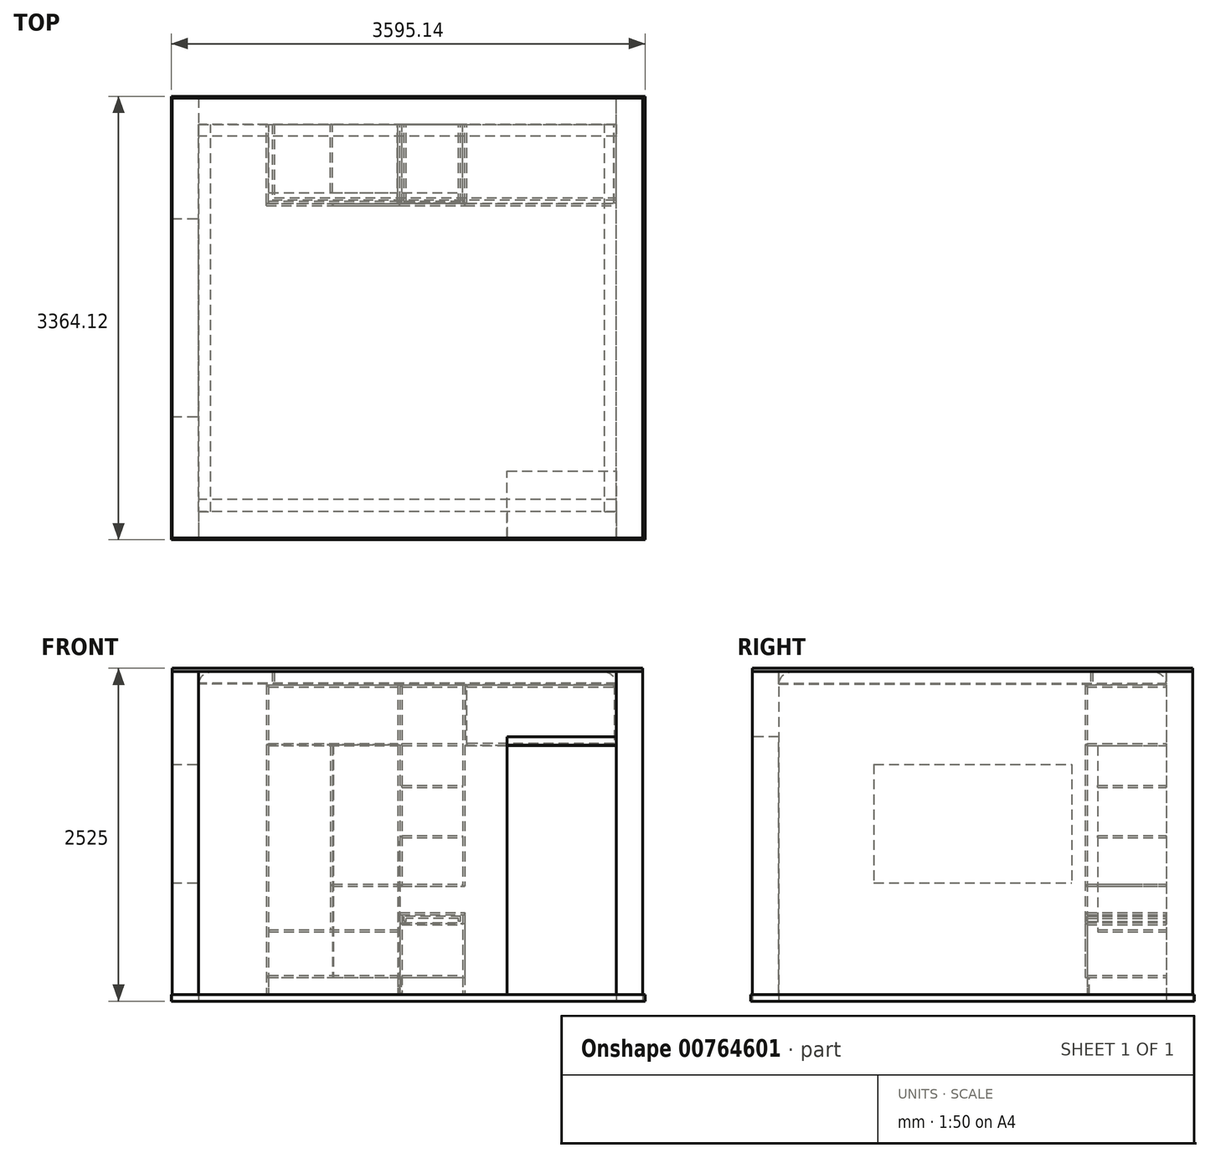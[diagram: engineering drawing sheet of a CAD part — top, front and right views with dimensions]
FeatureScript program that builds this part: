
annotation { "Feature Type Name" : "Feature", "Feature Type Description" : "" }
export const myFeature = defineFeature(function(context is Context, id is Id, definition is map)
    precondition{}
    {
        {
            var Q0;
            Q0=qCreatedBy(makeId("Top.planeOp"),FACE);
            var sketch = newSketch(context, id + "F0", { "sketchPlane" : qUnion([Q0])});
            skLineSegment(sketch, "E0.0.0", {"start": v(-1555, 1015.23) * mm, "end": v(1615, 1015.23) * mm});
            skLineSegment(sketch, "E0.0.1", {"start": v(1615, 1015.23) * mm, "end": v(1615, 1215.23) * mm});
            skLineSegment(sketch, "E0.0.2", {"start": v(1615, 1215.23) * mm, "end": v(-1555, 1215.23) * mm});
            skLineSegment(sketch, "E0.0.3", {"start": v(-1555, 1215.23) * mm, "end": v(-1555, 1015.23) * mm});
            skLineSegment(sketch, "E1.bottom", {"start": v(1815, 1215.23) * mm, "end": v(1615, 1215.23) * mm});
            skLineSegment(sketch, "E1.top", {"start": v(1815, -2124.77) * mm, "end": v(1615, -2124.77) * mm});
            skLineSegment(sketch, "E1.left", {"start": v(1815, 1215.23) * mm, "end": v(1815, -2124.77) * mm});
            skLineSegment(sketch, "E1.right", {"start": v(1615, 1215.23) * mm, "end": v(1615, -2124.77) * mm});
            skLineSegment(sketch, "E2.bottom", {"start": v(-1555, 1215.23) * mm, "end": v(-1755, 1215.23) * mm});
            skLineSegment(sketch, "E2.top", {"start": v(-1555, -2124.77) * mm, "end": v(-1755, -2124.77) * mm});
            skLineSegment(sketch, "E2.left", {"start": v(-1555, 1215.23) * mm, "end": v(-1555, -2124.77) * mm});
            skLineSegment(sketch, "E2.right", {"start": v(-1755, 1215.23) * mm, "end": v(-1755, -2124.77) * mm});
            skLineSegment(sketch, "E3.0.0", {"start": v(-1555, -2124.77) * mm, "end": v(1613.37, -2124.77) * mm});
            skLineSegment(sketch, "E3.0.1", {"start": v(1613.37, -2124.77) * mm, "end": v(1613.37, -1924.77) * mm});
            skLineSegment(sketch, "E3.0.2", {"start": v(1613.37, -1924.77) * mm, "end": v(-1555, -1924.77) * mm});
            skLineSegment(sketch, "E3.0.3", {"start": v(-1555, -1924.77) * mm, "end": v(-1555, -2124.77) * mm});
            skSolve(sketch);
        }
        {
            var Q0;
            {var subQ2=sQuery(id+"F0.wireOp",EDGE,"E1.bottom");Q0=makeQuery(id+"F0.imprint","IMPRINT",FACE,{"disambiguationData":[TD([[makeQuery(id+"F0.imprint","IMPRINT",EDGE,{"derivedFrom":subQ2}),1.0]])]});}
            var Q1;
            {var subQ5=sQuery(id+"F0.wireOp",EDGE,"E2.bottom");Q1=makeQuery(id+"F0.imprint","IMPRINT",FACE,{"disambiguationData":[TD([[makeQuery(id+"F0.imprint","IMPRINT",EDGE,{"derivedFrom":subQ5}),1.0]])]});}
            extrude(context, id + "F1", {"entities" : qUnion([Q0, Q1]), "depth" : 2500 * mm, "offsetDistance" : 25 * mm});
        }
        {
            var Q0;
            {var subQ0=sQuery(id+"F0.wireOp",EDGE,"E0.0.0");Q0=makeQuery(id+"F0.imprint","IMPRINT",FACE,{"disambiguationData":[TD([[makeQuery(id+"F0.imprint","IMPRINT",EDGE,{"derivedFrom":subQ0}),1.0]])]});}
            var Q1;
            Q1=makeQuery(id+"F0.imprint","IMPRINT",FACE,{"disambiguationData":[TD([[makeQuery(id+"F0.imprint","IMPRINT",EDGE,{"derivedFrom":sQuery(id+"F0.wireOp",EDGE,"E3.0.0")}),1.0]])]});
            extrude(context, id + "F2", {"entities" : qUnion([Q0, Q1]), "depth" : 2500 * mm, "offsetDistance" : 25 * mm});
        }
        {
            var Q0;
            Q0=makeQuery(id+"F1.opExtrude","SWEPT_FACE",FACE,{"disambiguationData":[OSD([sQuery(id+"F0.wireOp",EDGE,"E2.left"),sQuery(id+"F0.wireOp",EDGE,"E3.0.3")])]});
            var sketch = newSketch(context, id + "F3", { "sketchPlane" : qUnion([Q0])});
            skLineSegment(sketch, "E4.bottom", {"start": v(-1202.13, 1797) * mm, "end": v(297.87, 1797) * mm});
            skLineSegment(sketch, "E4.top", {"start": v(-1202.13, 897) * mm, "end": v(297.87, 897) * mm});
            skLineSegment(sketch, "E4.left", {"start": v(-1202.13, 1797) * mm, "end": v(-1202.13, 897) * mm});
            skLineSegment(sketch, "E4.right", {"start": v(297.87, 1797) * mm, "end": v(297.87, 897) * mm});
            skSolve(sketch);
        }
        {
            var Q0;
            Q0=makeQuery(id+"F3.imprint","IMPRINT",FACE,{"disambiguationData":[TD([[makeQuery(id+"F3.imprint","IMPRINT",EDGE,{"derivedFrom":sQuery(id+"F3.wireOp",EDGE,"E4.bottom")}),-1.0]])]});
            extrude(context, id + "F4", {"entities" : qUnion([Q0]), "operationType" : NewBodyOperationType.REMOVE, "oppositeDirection" : true, "depth" : 620 * mm, "offsetDistance" : 25 * mm});
        }
        {
            var Q0;
            {var subQ0=sQuery(id+"F0.wireOp",EDGE,"E0.0.0");Q0=makeQuery(id+"F0.imprint","IMPRINT",FACE,{"disambiguationData":[TD([[makeQuery(id+"F0.imprint","IMPRINT",EDGE,{"derivedFrom":subQ0}),1.0]])]});}
            var sketch = newSketch(context, id + "F5", { "sketchPlane" : qUnion([Q0])});
            skLineSegment(sketch, "E5.bottom", {"start": v(-1761.66, -2136.75) * mm, "end": v(1833.48, -2136.75) * mm});
            skLineSegment(sketch, "E5.top", {"start": v(-1761.66, 1227.37) * mm, "end": v(1833.48, 1227.37) * mm});
            skLineSegment(sketch, "E5.left", {"start": v(-1761.66, -2136.75) * mm, "end": v(-1761.66, 1227.37) * mm});
            skLineSegment(sketch, "E5.right", {"start": v(1833.48, -2136.75) * mm, "end": v(1833.48, 1227.37) * mm});
            skSolve(sketch);
        }
        {
            var Q0;
            Q0=makeQuery(id+"F5.imprint","IMPRINT",FACE,{"disambiguationData":[TD([[makeQuery(id+"F5.imprint","IMPRINT",EDGE,{"derivedFrom":sQuery(id+"F5.wireOp",EDGE,"E5.bottom")}),1.0]])]});
            extrude(context, id + "F6", {"entities" : qUnion([Q0]), "depth" : 50 * mm, "offsetDistance" : 25 * mm});
        }
        {
            var Q0;
            Q0=makeQuery(id+"F2.opExtrude","SWEPT_FACE",FACE,{"disambiguationData":[OSD([sQuery(id+"F0.wireOp",EDGE,"E0.0.0")])]});
            var sketch = newSketch(context, id + "F7", { "sketchPlane" : qUnion([Q0])});
            skLineSegment(sketch, "E6.bottom", {"start": v(-1555, 2500) * mm, "end": v(-1462.64, 2500) * mm});
            skLineSegment(sketch, "E6.left", {"start": v(-1555, 2500) * mm, "end": v(-1555, 2412.32) * mm});
            skFitSpline(sketch, "E7", {"points": [v(-1555, 2400.43) * mm, v(-1455, 2500) * mm], "startDerivative": vector(33.84, 289.83) * mm, "endDerivative": vector(27.08, 13.3) * mm});
            skArc(sketch, "E8.filletArc", {"start": v(-1555, 2412.32) * mm, "mid": v(-1554.18, 2411.42) * mm, "end": v(-1553.22, 2412.15) * mm});
            skArc(sketch, "E9.filletArc", {"start": v(-1462.48, 2498.21) * mm, "mid": v(-1461.75, 2499.18) * mm, "end": v(-1462.64, 2500) * mm});
            skLineSegment(sketch, "E10.bottom", {"start": v(1615, 2500) * mm, "end": v(1615, 2407.64) * mm});
            skLineSegment(sketch, "E10.left", {"start": v(1615, 2500) * mm, "end": v(1527.32, 2500) * mm});
            skFitSpline(sketch, "E11", {"points": [v(1515.43, 2500) * mm, v(1615, 2400) * mm], "startDerivative": vector(289.83, -33.84) * mm, "endDerivative": vector(13.3, -27.08) * mm});
            skArc(sketch, "E12.filletArc", {"start": v(1527.32, 2500) * mm, "mid": v(1526.42, 2499.18) * mm, "end": v(1527.15, 2498.22) * mm});
            skArc(sketch, "E13.filletArc", {"start": v(1613.22, 2407.48) * mm, "mid": v(1614.18, 2406.75) * mm, "end": v(1615, 2407.64) * mm});
            skSolve(sketch);
        }
        {
            var Q0;
            Q0 = qSketchRegion(id + "F7", true);
            extrude(context, id + "F8", {"entities" : qUnion([Q0]), "depth" : 2940 * mm, "offsetDistance" : 25 * mm});
        }
        {
            var Q0;
            Q0=makeQuery(id+"F1.opExtrude","SWEPT_FACE",FACE,{"disambiguationData":[OSD([sQuery(id+"F0.wireOp",EDGE,"E2.left"),sQuery(id+"F0.wireOp",EDGE,"E3.0.3")])]});
            var sketch = newSketch(context, id + "F9", { "sketchPlane" : qUnion([Q0])});
            skLineSegment(sketch, "E14.bottom", {"start": v(-1924.58, 2500) * mm, "end": v(-1832.23, 2500) * mm});
            skLineSegment(sketch, "E14.left", {"start": v(-1924.58, 2500) * mm, "end": v(-1924.58, 2412.32) * mm});
            skFitSpline(sketch, "E15", {"points": [v(-1924.58, 2400.43) * mm, v(-1824.58, 2500) * mm], "startDerivative": vector(33.84, 289.83) * mm, "endDerivative": vector(27.08, 13.3) * mm});
            skArc(sketch, "E16.filletArc", {"start": v(-1924.58, 2412.32) * mm, "mid": v(-1923.77, 2411.43) * mm, "end": v(-1922.8, 2412.15) * mm});
            skArc(sketch, "E17.filletArc", {"start": v(-1832.06, 2498.22) * mm, "mid": v(-1831.33, 2499.19) * mm, "end": v(-1832.23, 2500) * mm});
            skLineSegment(sketch, "E18.bottom", {"start": v(1014.88, 2500) * mm, "end": v(1014.88, 2407.64) * mm});
            skLineSegment(sketch, "E18.left", {"start": v(1014.88, 2500) * mm, "end": v(927.2, 2500) * mm});
            skFitSpline(sketch, "E19", {"points": [v(915.3, 2500) * mm, v(1014.88, 2400) * mm], "startDerivative": vector(289.83, -33.84) * mm, "endDerivative": vector(13.3, -27.08) * mm});
            skArc(sketch, "E20.filletArc", {"start": v(927.2, 2500) * mm, "mid": v(926.3, 2499.18) * mm, "end": v(927.03, 2498.22) * mm});
            skArc(sketch, "E21.filletArc", {"start": v(1013.1, 2407.48) * mm, "mid": v(1014.06, 2406.75) * mm, "end": v(1014.88, 2407.64) * mm});
            skSolve(sketch);
        }
        {
            var Q0;
            Q0 = qSketchRegion(id + "F9", true);
            extrude(context, id + "F10", {"entities" : qUnion([Q0]), "depth" : 3169.2 * mm, "offsetDistance" : 25 * mm});
        }
        {
            var Q0;
            Q0=makeQuery(id+"F2.opExtrude","SWEPT_FACE",FACE,{"disambiguationData":[OSD([sQuery(id+"F0.wireOp",EDGE,"E3.0.0")])]});
            var sketch = newSketch(context, id + "F11", { "sketchPlane" : qUnion([Q0])});
            skLineSegment(sketch, "E22.bottom", {"start": v(1613.37, 49.92) * mm, "end": v(785.99, 49.92) * mm});
            skLineSegment(sketch, "E22.top", {"start": v(1613.37, 2005.08) * mm, "end": v(785.99, 2005.08) * mm});
            skLineSegment(sketch, "E22.left", {"start": v(1613.37, 49.92) * mm, "end": v(1613.37, 2005.08) * mm});
            skLineSegment(sketch, "E22.right", {"start": v(785.99, 49.92) * mm, "end": v(785.99, 2005.08) * mm});
            skSolve(sketch);
        }
        {
            var Q0;
            Q0=makeQuery(id+"F11.imprint","IMPRINT",FACE,{"disambiguationData":[TD([[makeQuery(id+"F11.imprint","IMPRINT",EDGE,{"derivedFrom":sQuery(id+"F11.wireOp",EDGE,"E22.bottom")}),-1.0]])]});
            extrude(context, id + "F12", {"entities" : qUnion([Q0]), "operationType" : NewBodyOperationType.REMOVE, "oppositeDirection" : true, "depth" : 510 * mm, "offsetDistance" : 25 * mm});
        }
        {
            var Q0;
            Q0=makeQuery(id+"F2.opExtrude","CAP_FACE",FACE,{"disambiguationData":[OSD([sQuery(id+"F0.wireOp",EDGE,"E0.0.0"),sQuery(id+"F0.wireOp",EDGE,"E0.0.2"),sQuery(id+"F0.wireOp",EDGE,"E1.right"),sQuery(id+"F0.wireOp",EDGE,"E2.left")])],"isStart":false});
            var sketch = newSketch(context, id + "F13", { "sketchPlane" : qUnion([Q0])});
            skLineSegment(sketch, "E23.0", {"start": v(1815, 1215.23) * mm, "end": v(-1755, 1215.23) * mm});
            skLineSegment(sketch, "E24.0", {"start": v(1815, 1215.23) * mm, "end": v(1815, -2124.77) * mm});
            skLineSegment(sketch, "E25.0", {"start": v(-1755, -2124.77) * mm, "end": v(1815, -2124.77) * mm});
            skLineSegment(sketch, "E26.0", {"start": v(-1755, 1215.23) * mm, "end": v(-1755, -2124.77) * mm});
            skSolve(sketch);
        }
        {
            var Q0;
            Q0 = qSketchRegion(id + "F13", true);
            extrude(context, id + "F14", {"entities" : qUnion([Q0]), "depth" : 25 * mm, "offsetDistance" : 25 * mm});
        }
        {
            var Q0;
            Q0=makeQuery(id+"F2.opExtrude","SWEPT_FACE",FACE,{"disambiguationData":[OSD([sQuery(id+"F0.wireOp",EDGE,"E0.0.0")])]});
            var sketch = newSketch(context, id + "F15", { "sketchPlane" : qUnion([Q0])});
            skLineSegment(sketch, "E27", {"start": v(498.7, 98.2) * mm, "end": v(1598.7, 98.2) * mm});
            skLineSegment(sketch, "E28", {"start": v(-930.04, 98.4) * mm, "end": v(469.96, 98.4) * mm});
            skLineSegment(sketch, "E29", {"start": v(-930.56, 51.34) * mm, "end": v(-930.04, 1954.15) * mm});
            skLineSegment(sketch, "E30", {"start": v(-930.04, 1954.15) * mm, "end": v(-930.04, 2500) * mm});
            skSolve(sketch);
        }
        {
            var Q0;
            {var subQ0=sQuery(id+"F0.wireOp",EDGE,"E0.0.0");Q0=makeQuery(id+"F15.imprint","IMPRINT",FACE,{"disambiguationData":[TD([[makeQuery(id+"F15.imprint","IMPRINT",EDGE,{"derivedFrom":makeQuery(id+"F2.opExtrude","CAP_EDGE",EDGE,{"disambiguationData":[OSD([subQ0])],"isStart":true})}),1.0]])]});}
            var sketch = newSketch(context, id + "F16", { "sketchPlane" : qUnion([Q0])});
            skLineSegment(sketch, "E31.bottom", {"start": v(-1039.66, 2400.3) * mm, "end": v(-1023.66, 2400.3) * mm});
            skLineSegment(sketch, "E31.top", {"start": v(-1039.66, 50.3) * mm, "end": v(-1023.66, 50.3) * mm});
            skLineSegment(sketch, "E31.left", {"start": v(-1039.66, 2400.3) * mm, "end": v(-1039.66, 50.3) * mm});
            skLineSegment(sketch, "E31.right", {"start": v(-1023.66, 2400.3) * mm, "end": v(-1023.66, 50.3) * mm});
            skLineSegment(sketch, "E32.bottom", {"start": v(449.94, 2400.3) * mm, "end": v(466, 2400.3) * mm});
            skLineSegment(sketch, "E32.top", {"start": v(450, 50.3) * mm, "end": v(466, 50.3) * mm});
            skLineSegment(sketch, "E32.left", {"start": v(449.94, 2400.3) * mm, "end": v(449.98, 873.05) * mm});
            skLineSegment(sketch, "E32.right", {"start": v(466, 2400.3) * mm, "end": v(466, 873.05) * mm});
            skLineSegment(sketch, "E33.bottom", {"start": v(-1023.54, 1938) * mm, "end": v(-1023.54, 1954) * mm});
            skLineSegment(sketch, "E34.bottom", {"start": v(-1023.33, 2384.28) * mm, "end": v(-1023.33, 2400.28) * mm});
            skLineSegment(sketch, "E34.left", {"start": v(-1023.33, 2384.28) * mm, "end": v(-44.46, 2384.27) * mm});
            skLineSegment(sketch, "E34.right", {"start": v(-1023.33, 2400.28) * mm, "end": v(-44.38, 2400.27) * mm});
            skLineSegment(sketch, "E35.bottom", {"start": v(-1023.48, 180.4) * mm, "end": v(-1023.48, 196.4) * mm});
            skLineSegment(sketch, "E35.left", {"start": v(-1023.48, 180.4) * mm, "end": v(-45.21, 180.4) * mm});
            skLineSegment(sketch, "E35.right", {"start": v(-1023.48, 196.4) * mm, "end": v(-45.21, 196.4) * mm});
            skLineSegment(sketch, "E36.bottom", {"start": v(-43.86, 2400.3) * mm, "end": v(-27.86, 2400.3) * mm});
            skLineSegment(sketch, "E36.top", {"start": v(-43.86, 50.3) * mm, "end": v(-27.86, 50.3) * mm});
            skLineSegment(sketch, "E36.left", {"start": v(-43.86, 2400.3) * mm, "end": v(-43.86, 50.3) * mm});
            skLineSegment(sketch, "E36.right", {"start": v(-27.86, 2400.3) * mm, "end": v(-27.86, 50.3) * mm});
            skLineSegment(sketch, "E37.top", {"start": v(-44.6, 1937.98) * mm, "end": v(-44.6, 1953.98) * mm});
            skLineSegment(sketch, "E37.left", {"start": v(-1023.54, 1938) * mm, "end": v(-44.6, 1937.98) * mm});
            skLineSegment(sketch, "E37.right", {"start": v(-1023.54, 1954) * mm, "end": v(-44.6, 1953.98) * mm});
            skLineSegment(sketch, "E38.bottom", {"start": v(-11.33, 1621.98) * mm, "end": v(-11.33, 1637.98) * mm});
            skLineSegment(sketch, "E38.top", {"start": v(449.6, 1621.98) * mm, "end": v(449.6, 1637.98) * mm});
            skLineSegment(sketch, "E38.left", {"start": v(-11.33, 1621.98) * mm, "end": v(449.6, 1621.98) * mm});
            skLineSegment(sketch, "E38.right", {"start": v(-11.33, 1637.98) * mm, "end": v(449.6, 1637.98) * mm});
            skLineSegment(sketch, "E39.bottom", {"start": v(-11.33, 873) * mm, "end": v(-11.33, 889) * mm});
            skLineSegment(sketch, "E39.top", {"start": v(449.6, 873) * mm, "end": v(449.6, 889) * mm});
            skLineSegment(sketch, "E39.left", {"start": v(-11.33, 873) * mm, "end": v(449.6, 873) * mm});
            skLineSegment(sketch, "E39.right", {"start": v(-11.33, 889) * mm, "end": v(449.6, 889) * mm});
            skLineSegment(sketch, "E40.bottom", {"start": v(-27.77, 657) * mm, "end": v(-27.77, 673) * mm});
            skLineSegment(sketch, "E40.top", {"start": v(466.02, 657) * mm, "end": v(466.02, 673) * mm});
            skLineSegment(sketch, "E40.left", {"start": v(-27.77, 657) * mm, "end": v(466.02, 657) * mm});
            skLineSegment(sketch, "E40.right", {"start": v(-27.77, 673) * mm, "end": v(466.02, 673) * mm});
            skLineSegment(sketch, "E41.bottom", {"start": v(-27.72, 2400.3) * mm, "end": v(-11.63, 2400.3) * mm});
            skLineSegment(sketch, "E41.top", {"start": v(-27.72, 50.3) * mm, "end": v(-11.72, 50.3) * mm});
            skLineSegment(sketch, "E41.left", {"start": v(-27.72, 2400.3) * mm, "end": v(-27.72, 872.64) * mm});
            skLineSegment(sketch, "E41.right", {"start": v(-11.63, 2400.3) * mm, "end": v(-11.69, 872.64) * mm});
            skLineSegment(sketch, "E42.bottom", {"start": v(-538.34, 1937.41) * mm, "end": v(-538.34, 543.17) * mm});
            skLineSegment(sketch, "E42.top", {"start": v(-554.34, 1937.41) * mm, "end": v(-554.34, 543.17) * mm});
            skLineSegment(sketch, "E42.left", {"start": v(-538.34, 1937.41) * mm, "end": v(-554.34, 1937.41) * mm});
            skLineSegment(sketch, "E42.right", {"start": v(-538.34, 543.17) * mm, "end": v(-554.34, 543.17) * mm});
            skLineSegment(sketch, "E43.bottom", {"start": v(-1022.14, 541.4) * mm, "end": v(-44.34, 541.4) * mm});
            skLineSegment(sketch, "E43.top", {"start": v(-1022.14, 525.4) * mm, "end": v(-44.34, 525.4) * mm});
            skLineSegment(sketch, "E43.left", {"start": v(-1022.14, 541.4) * mm, "end": v(-1022.14, 525.4) * mm});
            skLineSegment(sketch, "E43.right", {"start": v(-44.34, 541.4) * mm, "end": v(-44.34, 525.4) * mm});
            skLineSegment(sketch, "E44", {"start": v(-45.21, 196.4) * mm, "end": v(-45.21, 180.4) * mm});
            skLineSegment(sketch, "E45.bottom", {"start": v(-11.33, 196.4) * mm, "end": v(448.57, 196.4) * mm});
            skLineSegment(sketch, "E45.top", {"start": v(-11.33, 180.4) * mm, "end": v(448.57, 180.4) * mm});
            skLineSegment(sketch, "E45.left", {"start": v(-11.33, 196.4) * mm, "end": v(-11.33, 180.4) * mm});
            skLineSegment(sketch, "E45.right", {"start": v(448.57, 196.4) * mm, "end": v(448.57, 180.4) * mm});
            skLineSegment(sketch, "E46", {"start": v(-44.38, 2400.27) * mm, "end": v(-44.46, 2384.27) * mm});
            skLineSegment(sketch, "E47.bottom", {"start": v(-11.1, 1937.99) * mm, "end": v(-11.1, 1953.99) * mm});
            skLineSegment(sketch, "E47.left", {"start": v(-11.1, 1937.99) * mm, "end": v(449.65, 1937.98) * mm});
            skLineSegment(sketch, "E47.right", {"start": v(-11.1, 1953.99) * mm, "end": v(449.73, 1953.98) * mm});
            skLineSegment(sketch, "E48", {"start": v(449.73, 1953.98) * mm, "end": v(449.65, 1937.98) * mm});
            skLineSegment(sketch, "E49.bottom", {"start": v(-11.58, 2384.27) * mm, "end": v(-11.58, 2400.27) * mm});
            skLineSegment(sketch, "E49.left", {"start": v(-11.58, 2384.27) * mm, "end": v(449.35, 2384.26) * mm});
            skLineSegment(sketch, "E49.right", {"start": v(-11.58, 2400.27) * mm, "end": v(449.43, 2400.26) * mm});
            skLineSegment(sketch, "E50", {"start": v(449.43, 2400.26) * mm, "end": v(449.35, 2384.26) * mm});
            skLineSegment(sketch, "E51.trimOffspring", {"start": v(449.98, 656.59) * mm, "end": v(450, 50.3) * mm});
            skLineSegment(sketch, "E52.trimOffspring", {"start": v(466, 656.59) * mm, "end": v(466, 50.3) * mm});
            skLineSegment(sketch, "E53.trimOffspring", {"start": v(-11.7, 656.86) * mm, "end": v(-11.72, 50.3) * mm});
            skPoint(sketch, "E54", {"position": v(-27.72, 656.81) * mm});
            skLineSegment(sketch, "E55.trimOffspring", {"start": v(-27.72, 656.81) * mm, "end": v(-27.72, 50.3) * mm});
            skLineSegment(sketch, "E56", {"start": v(-27.72, 656.81) * mm, "end": v(-11.7, 656.86) * mm});
            skLineSegment(sketch, "E57", {"start": v(-11.69, 872.64) * mm, "end": v(-27.72, 872.64) * mm});
            skLineSegment(sketch, "E58", {"start": v(466, 873.05) * mm, "end": v(449.98, 873.05) * mm});
            skLineSegment(sketch, "E59.bottom", {"start": v(-11.33, 1238.98) * mm, "end": v(-11.33, 1254.98) * mm});
            skLineSegment(sketch, "E59.top", {"start": v(449.6, 1238.98) * mm, "end": v(449.6, 1254.98) * mm});
            skLineSegment(sketch, "E59.left", {"start": v(-11.33, 1238.98) * mm, "end": v(449.6, 1238.98) * mm});
            skLineSegment(sketch, "E59.right", {"start": v(-11.33, 1254.98) * mm, "end": v(449.6, 1254.98) * mm});
            skLineSegment(sketch, "E60.bottom", {"start": v(-537.04, 872.5) * mm, "end": v(-537.04, 888.5) * mm});
            skLineSegment(sketch, "E60.top", {"start": v(-44.46, 872.5) * mm, "end": v(-44.46, 888.5) * mm});
            skLineSegment(sketch, "E60.left", {"start": v(-537.04, 872.5) * mm, "end": v(-44.46, 872.5) * mm});
            skLineSegment(sketch, "E60.right", {"start": v(-537.04, 888.5) * mm, "end": v(-44.46, 888.5) * mm});
            skLineSegment(sketch, "E61", {"start": v(449.98, 656.59) * mm, "end": v(466, 656.59) * mm});
            skLineSegment(sketch, "E62.bottom", {"start": v(-11.3, 580.01) * mm, "end": v(-11.3, 596.01) * mm});
            skLineSegment(sketch, "E62.top", {"start": v(449.64, 580) * mm, "end": v(449.64, 596) * mm});
            skLineSegment(sketch, "E62.left", {"start": v(-11.3, 580.01) * mm, "end": v(449.64, 580) * mm});
            skLineSegment(sketch, "E62.right", {"start": v(-11.3, 596.01) * mm, "end": v(449.64, 596) * mm});
            skSolve(sketch);
        }
        {
            var Q0;
            Q0=makeQuery(id+"F16.imprint","IMPRINT",FACE,{"disambiguationData":[TD([[makeQuery(id+"F16.imprint","IMPRINT",EDGE,{"derivedFrom":sQuery(id+"F16.wireOp",EDGE,"E31.bottom")}),-1.0]])]});
            var Q1;
            {var subQ0=sQuery(id+"F16.wireOp",EDGE,"E36.top");Q1=makeQuery(id+"F16.imprint","IMPRINT",FACE,{"disambiguationData":[TD([[makeQuery(id+"F16.imprint","IMPRINT",EDGE,{"derivedFrom":subQ0}),1.0]])]});}
            var Q2;
            {var subQ5=sQuery(id+"F16.wireOp",EDGE,"E41.top");Q2=makeQuery(id+"F16.imprint","IMPRINT",FACE,{"disambiguationData":[TD([[makeQuery(id+"F16.imprint","IMPRINT",EDGE,{"derivedFrom":subQ5}),1.0]])]});}
            var Q3;
            Q3=makeQuery(id+"F16.imprint","IMPRINT",FACE,{"disambiguationData":[TD([[makeQuery(id+"F16.imprint","IMPRINT",EDGE,{"derivedFrom":sQuery(id+"F16.wireOp",EDGE,"E32.bottom")}),-1.0]])]});
            var Q4;
            Q4=makeQuery(id+"F16.imprint","IMPRINT",FACE,{"disambiguationData":[TD([[makeQuery(id+"F16.imprint","IMPRINT",EDGE,{"derivedFrom":sQuery(id+"F16.wireOp",EDGE,"E45.bottom")}),-1.0]])]});
            var Q5;
            Q5=makeQuery(id+"F16.imprint","IMPRINT",FACE,{"disambiguationData":[TD([[makeQuery(id+"F16.imprint","IMPRINT",EDGE,{"derivedFrom":sQuery(id+"F16.wireOp",EDGE,"E35.bottom")}),-1.0]])]});
            var Q6;
            Q6=makeQuery(id+"F16.imprint","IMPRINT",FACE,{"disambiguationData":[TD([[makeQuery(id+"F16.imprint","IMPRINT",EDGE,{"derivedFrom":sQuery(id+"F16.wireOp",EDGE,"E34.bottom")}),-1.0]])]});
            var Q7;
            Q7=makeQuery(id+"F16.imprint","IMPRINT",FACE,{"disambiguationData":[TD([[makeQuery(id+"F16.imprint","IMPRINT",EDGE,{"derivedFrom":sQuery(id+"F16.wireOp",EDGE,"E49.bottom")}),-1.0]])]});
            var Q8;
            Q8=makeQuery(id+"F16.imprint","IMPRINT",FACE,{"disambiguationData":[TD([[makeQuery(id+"F16.imprint","IMPRINT",EDGE,{"derivedFrom":sQuery(id+"F16.wireOp",EDGE,"E33.bottom")}),-1.0]])]});
            var Q9;
            Q9=makeQuery(id+"F16.imprint","IMPRINT",FACE,{"disambiguationData":[TD([[makeQuery(id+"F16.imprint","IMPRINT",EDGE,{"derivedFrom":sQuery(id+"F16.wireOp",EDGE,"E47.bottom")}),-1.0]])]});
            var Q10;
            Q10=makeQuery(id+"F16.imprint","IMPRINT",FACE,{"disambiguationData":[TD([[makeQuery(id+"F16.imprint","IMPRINT",EDGE,{"derivedFrom":sQuery(id+"F16.wireOp",EDGE,"E41.bottom")}),-1.0]])]});
            var Q11;
            Q11=makeQuery(id+"F16.imprint","IMPRINT",FACE,{"disambiguationData":[TD([[makeQuery(id+"F16.imprint","IMPRINT",EDGE,{"derivedFrom":sQuery(id+"F16.wireOp",EDGE,"E39.bottom")}),-1.0]])]});
            var Q12;
            Q12=makeQuery(id+"F16.imprint","IMPRINT",FACE,{"disambiguationData":[TD([[makeQuery(id+"F16.imprint","IMPRINT",EDGE,{"derivedFrom":sQuery(id+"F16.wireOp",EDGE,"E32.top")}),1.0]])]});
            var Q13;
            {var subQ3=sQuery(id+"F16.wireOp",EDGE,"E40.bottom");Q13=makeQuery(id+"F16.imprint","IMPRINT",FACE,{"disambiguationData":[TD([[makeQuery(id+"F16.imprint","IMPRINT",EDGE,{"derivedFrom":subQ3}),-1.0]])]});}
            var Q14;
            Q14=makeQuery(id+"F16.imprint","IMPRINT",FACE,{"disambiguationData":[TD([[makeQuery(id+"F16.imprint","IMPRINT",EDGE,{"derivedFrom":sQuery(id+"F16.wireOp",EDGE,"E62.bottom")}),-1.0]])]});
            extrude(context, id + "F17", {"entities" : qUnion([Q0, Q1, Q2, Q3, Q4, Q5, Q6, Q7, Q8, Q9, Q10, Q11, Q12, Q13, Q14]), "depth" : 600 * mm, "offsetDistance" : 25 * mm});
        }
        {
            var Q0;
            Q0=makeQuery(id+"F16.imprint","IMPRINT",FACE,{"disambiguationData":[TD([[makeQuery(id+"F16.imprint","IMPRINT",EDGE,{"derivedFrom":sQuery(id+"F16.wireOp",EDGE,"E43.bottom")}),-1.0]])]});
            var Q1;
            Q1=makeQuery(id+"F16.imprint","IMPRINT",FACE,{"disambiguationData":[TD([[makeQuery(id+"F16.imprint","IMPRINT",EDGE,{"derivedFrom":sQuery(id+"F16.wireOp",EDGE,"E42.bottom")}),-1.0]])]});
            var Q2;
            Q2=makeQuery(id+"F16.imprint","IMPRINT",FACE,{"disambiguationData":[TD([[makeQuery(id+"F16.imprint","IMPRINT",EDGE,{"derivedFrom":sQuery(id+"F16.wireOp",EDGE,"E38.bottom")}),-1.0]])]});
            var Q3;
            Q3=makeQuery(id+"F16.imprint","IMPRINT",FACE,{"disambiguationData":[TD([[makeQuery(id+"F16.imprint","IMPRINT",EDGE,{"derivedFrom":sQuery(id+"F16.wireOp",EDGE,"E59.bottom")}),-1.0]])]});
            var Q4;
            Q4=makeQuery(id+"F16.imprint","IMPRINT",FACE,{"disambiguationData":[TD([[makeQuery(id+"F16.imprint","IMPRINT",EDGE,{"derivedFrom":sQuery(id+"F16.wireOp",EDGE,"E60.bottom")}),-1.0]])]});
            extrude(context, id + "F18", {"entities" : qUnion([Q0, Q1, Q2, Q3, Q4]), "depth" : 520 * mm, "offsetDistance" : 25 * mm});
        }
        {
            var Q0;
            Q0=makeQuery(id+"F16.imprint","IMPRINT",FACE,{"disambiguationData":[TD([[makeQuery(id+"F16.imprint","IMPRINT",EDGE,{"derivedFrom":sQuery(id+"F16.wireOp",EDGE,"E31.bottom")}),1.0]])]});
            var sketch = newSketch(context, id + "F19", { "sketchPlane" : qUnion([Q0])});
            skLineSegment(sketch, "E63.0.0", {"start": v(482.33, 2384.3) * mm, "end": v(1596.28, 2384.3) * mm});
            skLineSegment(sketch, "E63.0.1", {"start": v(1596.28, 2384.3) * mm, "end": v(1596.28, 2400.3) * mm});
            skLineSegment(sketch, "E63.0.2", {"start": v(1596.28, 2400.3) * mm, "end": v(482.33, 2400.3) * mm});
            skLineSegment(sketch, "E63.0.3", {"start": v(482.33, 2400.3) * mm, "end": v(482.33, 2384.3) * mm});
            skLineSegment(sketch, "E64.0.0", {"start": v(466.1, 2400.3) * mm, "end": v(466.1, 1937.9) * mm});
            skLineSegment(sketch, "E64.0.1", {"start": v(466.1, 1937.9) * mm, "end": v(482.1, 1937.9) * mm});
            skLineSegment(sketch, "E64.0.2", {"start": v(482.1, 1937.9) * mm, "end": v(482.1, 2400.3) * mm});
            skLineSegment(sketch, "E64.0.3", {"start": v(482.1, 2400.3) * mm, "end": v(466.1, 2400.3) * mm});
            skLineSegment(sketch, "E65.0.0", {"start": v(1597.76, 2400.3) * mm, "end": v(1597.76, 1937.95) * mm});
            skLineSegment(sketch, "E65.0.1", {"start": v(1597.76, 1937.95) * mm, "end": v(1613.76, 1937.95) * mm});
            skLineSegment(sketch, "E65.0.2", {"start": v(1613.76, 1937.95) * mm, "end": v(1613.76, 2400.3) * mm});
            skLineSegment(sketch, "E65.0.3", {"start": v(1613.76, 2400.3) * mm, "end": v(1597.76, 2400.3) * mm});
            skLineSegment(sketch, "E66.0.0", {"start": v(482.28, 1937.98) * mm, "end": v(1597.13, 1937.98) * mm});
            skLineSegment(sketch, "E66.0.1", {"start": v(1597.13, 1937.98) * mm, "end": v(1597.13, 1953.98) * mm});
            skLineSegment(sketch, "E66.0.2", {"start": v(1597.13, 1953.98) * mm, "end": v(482.28, 1953.98) * mm});
            skLineSegment(sketch, "E66.0.3", {"start": v(482.28, 1953.98) * mm, "end": v(482.28, 1937.98) * mm});
            skSolve(sketch);
        }
        {
            var Q0;
            Q0 = qSketchRegion(id + "F19", true);
            extrude(context, id + "F20", {"entities" : qUnion([Q0]), "depth" : 600 * mm, "offsetDistance" : 25 * mm});
        }
        {
            var Q0;
            Q0=makeQuery(id+"F17.opExtrude","SWEPT_FACE",FACE,{"disambiguationData":[OSD([sQuery(id+"F16.wireOp",EDGE,"E36.left")])]});
            var sketch = newSketch(context, id + "F21", { "sketchPlane" : qUnion([Q0])});
            skLineSegment(sketch, "E67.bottom", {"start": v(-431.22, 180.59) * mm, "end": v(-415.22, 180.59) * mm});
            skLineSegment(sketch, "E67.top", {"start": v(-431.22, 49.78) * mm, "end": v(-415.22, 49.78) * mm});
            skLineSegment(sketch, "E67.left", {"start": v(-431.22, 180.59) * mm, "end": v(-431.22, 49.78) * mm});
            skLineSegment(sketch, "E67.right", {"start": v(-415.22, 180.59) * mm, "end": v(-415.22, 49.78) * mm});
            skSolve(sketch);
        }
        {
            var Q0;
            {var subQ0=sQuery(id+"F21.wireOp",EDGE,"E67.left");var subQ1=sQuery(id+"F21.wireOp",EDGE,"E67.bottom");var subQ2=makeQuery(id+"F21.imprint","INTERSECT",VERTEX,{"derivedFrom":[subQ1,subQ0]});Q0=makeQuery(id+"F21.imprint","IMPRINT",FACE,{"disambiguationData":[TD([[makeQuery(id+"F21.imprint","IMPRINT",EDGE,{"disambiguationData":[TD([[subQ2,-1.0]])],"derivedFrom":subQ1}),-1.0]])]});}
            extrude(context, id + "F22", {"entities" : qUnion([Q0]), "operationType" : NewBodyOperationType.REMOVE, "oppositeDirection" : true, "depth" : 25 * mm, "offsetDistance" : 25 * mm});
        }
        {
            var Q0;
            {var subQ0=sQuery(id+"F21.wireOp",EDGE,"E67.left");var subQ1=sQuery(id+"F21.wireOp",EDGE,"E67.bottom");var subQ2=makeQuery(id+"F21.imprint","INTERSECT",VERTEX,{"derivedFrom":[subQ1,subQ0]});Q0=makeQuery(id+"F21.imprint","IMPRINT",FACE,{"disambiguationData":[TD([[makeQuery(id+"F21.imprint","IMPRINT",EDGE,{"disambiguationData":[TD([[subQ2,-1.0]])],"derivedFrom":subQ1}),-1.0]])]});}
            extrude(context, id + "F23", {"entities" : qUnion([Q0]), "depth" : 979.7 * mm, "offsetDistance" : 25 * mm, "hasSecondDirection" : true, "secondDirectionOppositeDirection" : true, "secondDirectionDepth" : 493.8 * mm});
        }
        {
            var Q0;
            Q0=makeQuery(id+"F16.imprint","IMPRINT",FACE,{"disambiguationData":[TD([[makeQuery(id+"F16.imprint","IMPRINT",EDGE,{"derivedFrom":sQuery(id+"F16.wireOp",EDGE,"E31.bottom")}),1.0]])]});
            var sketch = newSketch(context, id + "F24", { "sketchPlane" : qUnion([Q0])});
            skLineSegment(sketch, "E68.0", {"start": v(-930.04, 2495) * mm, "end": v(-1550, 2495) * mm});
            skLineSegment(sketch, "E68.1", {"start": v(1610, 2495) * mm, "end": v(-930.04, 2495) * mm});
            skLineSegment(sketch, "E68.2", {"start": v(-1550, 2495) * mm, "end": v(-1550, 5) * mm});
            skLineSegment(sketch, "E68.3", {"start": v(-1550, 5) * mm, "end": v(1610, 5) * mm});
            skLineSegment(sketch, "E68.4", {"start": v(1610, 5) * mm, "end": v(1610, 2495) * mm});
            skLineSegment(sketch, "E69.0", {"start": v(434.17, 604.81) * mm, "end": v(434.21, 644.78) * mm});
            skLineSegment(sketch, "E69.1", {"start": v(434.17, 604.81) * mm, "end": v(418.17, 604.81) * mm});
            skLineSegment(sketch, "E69.2", {"start": v(4.07, 604.81) * mm, "end": v(4.21, 644.78) * mm});
            skLineSegment(sketch, "E69.3", {"start": v(434.21, 644.78) * mm, "end": v(4.21, 644.78) * mm});
            skLineSegment(sketch, "E70.0", {"start": v(418.17, 604.81) * mm, "end": v(418.2, 628.78) * mm});
            skLineSegment(sketch, "E70.2", {"start": v(20.07, 604.81) * mm, "end": v(20.16, 628.78) * mm});
            skLineSegment(sketch, "E70.3", {"start": v(418.2, 628.78) * mm, "end": v(20.16, 628.78) * mm});
            skLineSegment(sketch, "E71.trimOffspring", {"start": v(20.07, 604.81) * mm, "end": v(4.07, 604.81) * mm});
            skSolve(sketch);
        }
        {
            var Q0;
            Q0=makeQuery(id+"F24.imprint","IMPRINT",FACE,{"disambiguationData":[TD([[makeQuery(id+"F24.imprint","IMPRINT",EDGE,{"derivedFrom":sQuery(id+"F24.wireOp",EDGE,"E69.0")}),1.0]])]});
            extrude(context, id + "F25", {"entities" : qUnion([Q0]), "depth" : 600 * mm, "offsetDistance" : 25 * mm});
        }
        {
            var Q0;
            {var subQ0=sQuery(id+"F0.wireOp",EDGE,"E0.0.0");Q0=makeQuery(id+"F15.imprint","IMPRINT",FACE,{"disambiguationData":[TD([[makeQuery(id+"F15.imprint","IMPRINT",EDGE,{"derivedFrom":makeQuery(id+"F2.opExtrude","CAP_EDGE",EDGE,{"disambiguationData":[OSD([subQ0])],"isStart":true})}),1.0]])]});}
            cPlane(context, id + "F26", {"entities" : qUnion([Q0]), "cplaneType" : CPlaneType.OFFSET, "offset" : 600.5 * mm, "width" : 150 * mm, "height" : 150 * mm});
        }
        {
            var Q0;
            Q0=qCreatedBy(id+"F26.planeOp",FACE);
            var sketch = newSketch(context, id + "F27", { "sketchPlane" : qUnion([Q0])});
            skLineSegment(sketch, "E72.0", {"start": v(-1039.59, 1946.81) * mm, "end": v(-28.66, 1946.8) * mm});
            skLineSegment(sketch, "E73.0", {"start": v(-1039.38, 2400.28) * mm, "end": v(-28.44, 2400.27) * mm});
            skLineSegment(sketch, "E74", {"start": v(-1039.38, 2400.28) * mm, "end": v(-1039.59, 1946.81) * mm});
            skLineSegment(sketch, "E75", {"start": v(-28.44, 2400.27) * mm, "end": v(-28.66, 1946.8) * mm});
            skLineSegment(sketch, "E76.0", {"start": v(-1040.38, 180.5) * mm, "end": v(-539.22, 180.5) * mm});
            skLineSegment(sketch, "E77.0", {"start": v(-1039.56, 1945.81) * mm, "end": v(-538.32, 1945.8) * mm});
            skLineSegment(sketch, "E78", {"start": v(-1039.56, 1945.81) * mm, "end": v(-1040.38, 180.5) * mm});
            skLineSegment(sketch, "E79", {"start": v(-538.32, 1945.8) * mm, "end": v(-539.22, 180.5) * mm});
            skLineSegment(sketch, "E80.0", {"start": v(-532.33, 180.5) * mm, "end": v(-29.49, 180.5) * mm});
            skLineSegment(sketch, "E81.0", {"start": v(-531.51, 1945.8) * mm, "end": v(-28.6, 1945.8) * mm});
            skLineSegment(sketch, "E82", {"start": v(-531.51, 1945.8) * mm, "end": v(-532.33, 180.5) * mm});
            skLineSegment(sketch, "E83", {"start": v(-28.6, 1945.8) * mm, "end": v(-29.49, 180.5) * mm});
            skLineSegment(sketch, "E84.0", {"start": v(-27.4, 872.66) * mm, "end": v(464.65, 872.65) * mm});
            skLineSegment(sketch, "E85.0", {"start": v(-26.69, 2400.24) * mm, "end": v(465.42, 2400.24) * mm});
            skLineSegment(sketch, "E86", {"start": v(-26.69, 2400.24) * mm, "end": v(-27.4, 872.66) * mm});
            skLineSegment(sketch, "E87", {"start": v(465.42, 2400.24) * mm, "end": v(464.65, 872.65) * mm});
            skLineSegment(sketch, "E88.0", {"start": v(466.4, 1940.6) * mm, "end": v(1612.48, 1940.59) * mm});
            skLineSegment(sketch, "E89.0", {"start": v(466.62, 2400.24) * mm, "end": v(1612.71, 2400.22) * mm});
            skLineSegment(sketch, "E90", {"start": v(466.62, 2400.24) * mm, "end": v(466.4, 1940.6) * mm});
            skLineSegment(sketch, "E91", {"start": v(1612.71, 2400.22) * mm, "end": v(1612.48, 1940.59) * mm});
            skLineSegment(sketch, "E92.0", {"start": v(-26.3, 180.5) * mm, "end": v(465.15, 180.5) * mm});
            skLineSegment(sketch, "E93.0", {"start": v(-26.1, 587.86) * mm, "end": v(465.35, 587.85) * mm});
            skLineSegment(sketch, "E94", {"start": v(-26.1, 587.86) * mm, "end": v(-26.3, 180.5) * mm});
            skLineSegment(sketch, "E95", {"start": v(465.35, 587.85) * mm, "end": v(465.15, 180.5) * mm});
            skLineSegment(sketch, "E96.0", {"start": v(-26.1, 590.16) * mm, "end": v(465.34, 590.15) * mm});
            skLineSegment(sketch, "E97.0", {"start": v(-26.07, 672.01) * mm, "end": v(465.38, 672) * mm});
            skLineSegment(sketch, "E98", {"start": v(-26.07, 672.01) * mm, "end": v(-26.1, 590.16) * mm});
            skLineSegment(sketch, "E99", {"start": v(465.38, 672) * mm, "end": v(465.34, 590.15) * mm});
            skSolve(sketch);
        }
        {
            var Q0;
            Q0 = qSketchRegion(id + "F27", true);
            extrude(context, id + "F28", {"entities" : qUnion([Q0]), "depth" : 16 * mm, "offsetDistance" : 25 * mm});
        }
        {
            var Q0;
            Q0=makeQuery(id+"F17.opExtrude","SWEPT_FACE",FACE,{"disambiguationData":[OSD([sQuery(id+"F16.wireOp",EDGE,"E34.right")])]});
            var sketch = newSketch(context, id + "F29", { "sketchPlane" : qUnion([Q0])});
            skLineSegment(sketch, "E100.bottom", {"start": v(-994.46, 1015.23) * mm, "end": v(-978.46, 1015.23) * mm});
            skLineSegment(sketch, "E100.top", {"start": v(-994.46, 441.13) * mm, "end": v(-978.46, 441.13) * mm});
            skLineSegment(sketch, "E100.left", {"start": v(-994.46, 1015.23) * mm, "end": v(-994.46, 441.13) * mm});
            skLineSegment(sketch, "E100.right", {"start": v(-978.46, 1015.23) * mm, "end": v(-978.46, 441.13) * mm});
            skLineSegment(sketch, "E101.bottom", {"start": v(-994.46, 441.13) * mm, "end": v(-994.46, 457.13) * mm});
            skLineSegment(sketch, "E101.top", {"start": v(1613.62, 441.13) * mm, "end": v(1613.62, 457.13) * mm});
            skLineSegment(sketch, "E101.left", {"start": v(-994.46, 441.13) * mm, "end": v(1613.62, 441.13) * mm});
            skLineSegment(sketch, "E101.right", {"start": v(-994.46, 457.13) * mm, "end": v(1613.62, 457.13) * mm});
            skSolve(sketch);
        }
        {
            var Q0;
            Q0 = qSketchRegion(id + "F29", true);
            extrude(context, id + "F30", {"entities" : qUnion([Q0]), "depth" : 100 * mm, "offsetDistance" : 25 * mm});
        }
    });
